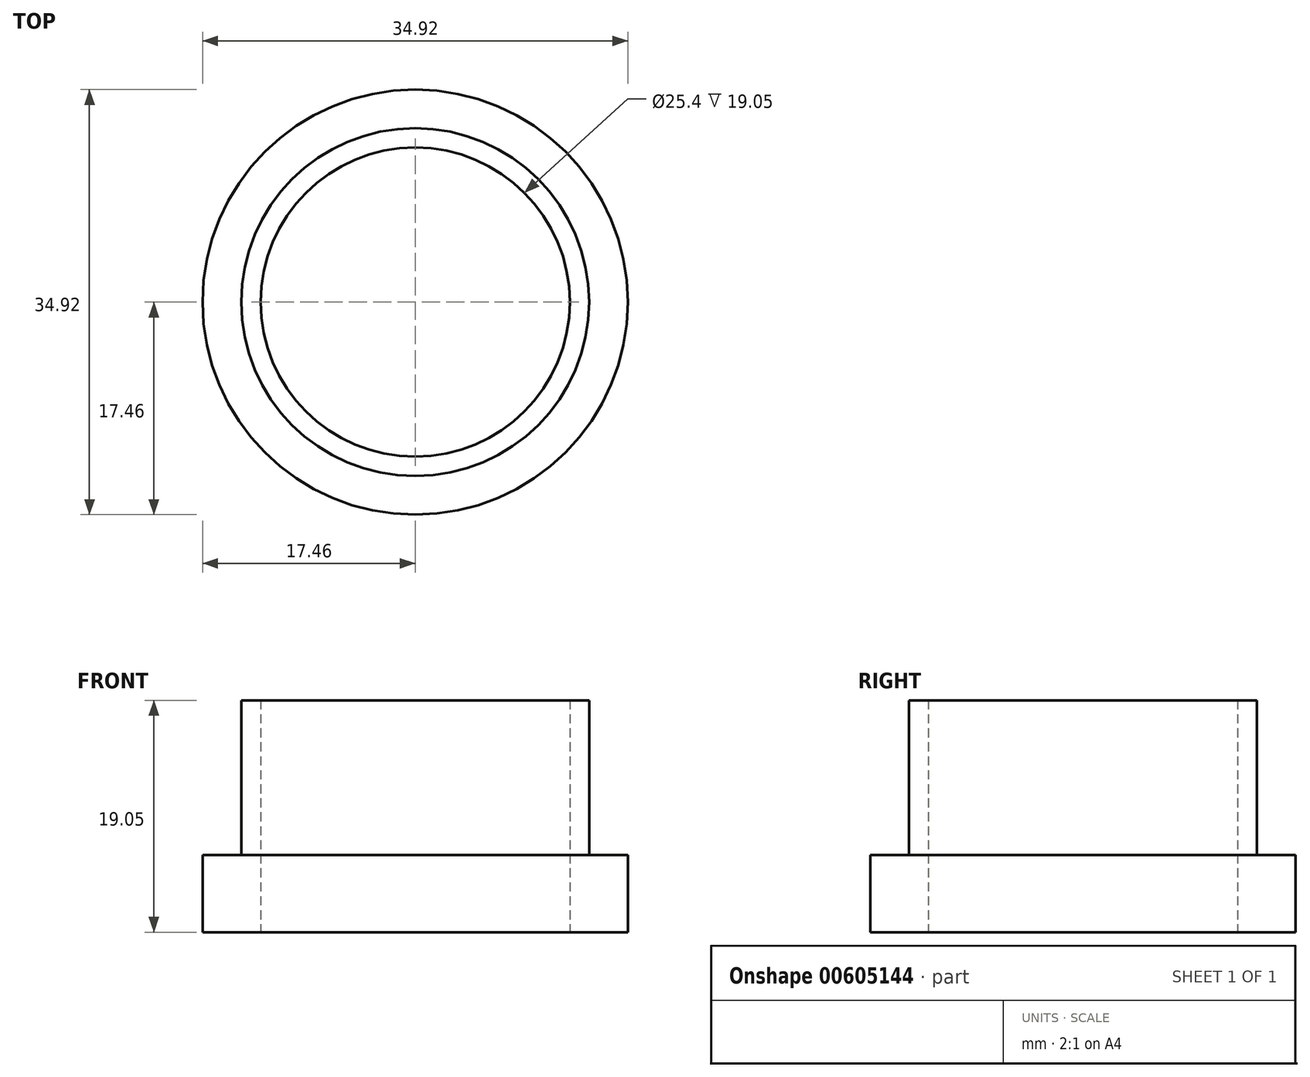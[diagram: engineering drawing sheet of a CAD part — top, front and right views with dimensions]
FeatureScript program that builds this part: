
annotation { "Feature Type Name" : "Feature", "Feature Type Description" : "" }
export const myFeature = defineFeature(function(context is Context, id is Id, definition is map)
    precondition{}
    {
        {
            var Q0;
            Q0=qCreatedBy(makeId("Top.planeOp"),FACE);
            var sketch = newSketch(context, id + "F0", { "sketchPlane" : qUnion([Q0])});
            skLineSegment(sketch, "E0", {"start": v(0, 0) * mm, "end": v(12.7, 0) * mm});
            skCircle(sketch, "E1", {"center": v(0, 0) * mm, "radius": 12.7 * mm});
            skCircle(sketch, "E2.0", {"center": v(0, 0) * mm, "radius": 14.29 * mm});
            skSolve(sketch);
        }
        {
            var Q0;
            Q0=qCreatedBy(makeId("Top.planeOp"),FACE);
            var sketch = newSketch(context, id + "F1", { "sketchPlane" : qUnion([Q0])});
            skSolve(sketch);
        }
        {
            var Q0;
            Q0=qSketchRegion(id+"F1",true);
            var Q1;
            Q1=makeQuery(id+"F0.imprint","IMPRINT",FACE,{"disambiguationData":[TD([[makeQuery(id+"F0.imprint","IMPRINT",EDGE,{"derivedFrom":sQuery(id+"F0.wireOp",EDGE,"E1")}),-1.0]])]});
            extrude(context, id + "F2", {"entities" : qUnion([Q0, Q1]), "depth" : 19.05 * mm, "offsetDistance" : 25.4 * mm});
        }
        {
            var Q0;
            Q0 = qSketchRegion(id + "F0", true);
            var sketch = newSketch(context, id + "F3", { "sketchPlane" : qUnion([Q0])});
            skCircle(sketch, "E3.0", {"center": v(0, 0) * mm, "radius": 17.46 * mm});
            skSolve(sketch);
        }
        {
            var Q0;
            Q0=makeQuery(id+"F3.imprint","IMPRINT",FACE,{"disambiguationData":[TD([[makeQuery(id+"F3.imprint","IMPRINT",EDGE,{"derivedFrom":sQuery(id+"F3.wireOp",EDGE,"E3.0")}),1.0]])]});
            var Q1;
            Q1=sQuery(id+"F3.wireOp",EDGE,"E3.0");
            var Q2;
            Q2=sQuery(id+"F0.wireOp",EDGE,"E2.0");
            extrude(context, id + "F4", {"entities" : qUnion([Q0]), "operationType" : NewBodyOperationType.ADD, "surfaceEntities" : qUnion([Q1, Q2]), "depth" : 6.35 * mm, "offsetDistance" : 25.4 * mm});
        }
    });
